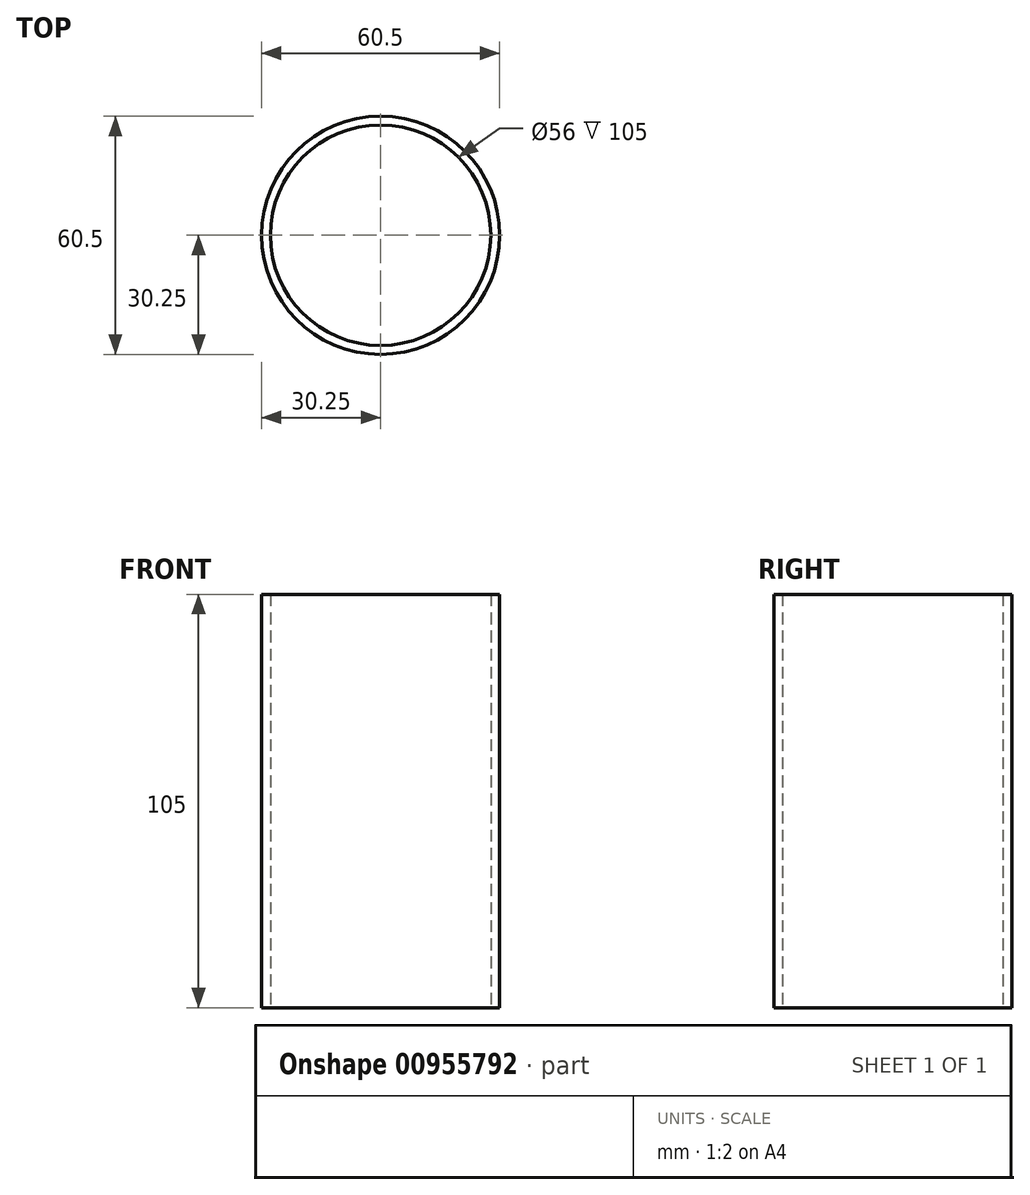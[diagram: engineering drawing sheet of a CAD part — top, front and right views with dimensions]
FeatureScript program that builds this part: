
annotation { "Feature Type Name" : "Feature", "Feature Type Description" : "" }
export const myFeature = defineFeature(function(context is Context, id is Id, definition is map)
    precondition{}
    {
        {
            var Q0;
            Q0=qCreatedBy(makeId("Top.planeOp"),FACE);
            var sketch = newSketch(context, id + "F0", { "sketchPlane" : qUnion([Q0])});
            skCircle(sketch, "E0", {"center": v(0, 0) * mm, "radius": 30.25 * mm});
            skCircle(sketch, "E1", {"center": v(0, 0) * mm, "radius": 28 * mm});
            skSolve(sketch);
        }
        {
            var Q0;
            Q0=makeQuery(id+"F0.imprint","IMPRINT",FACE,{"disambiguationData":[TD([[makeQuery(id+"F0.imprint","IMPRINT",EDGE,{"derivedFrom":sQuery(id+"F0.wireOp",EDGE,"E0")}),1.0]])]});
            extrude(context, id + "F1", {"entities" : qUnion([Q0]), "depth" : 105 * mm, "offsetDistance" : 25 * mm});
        }
    });
